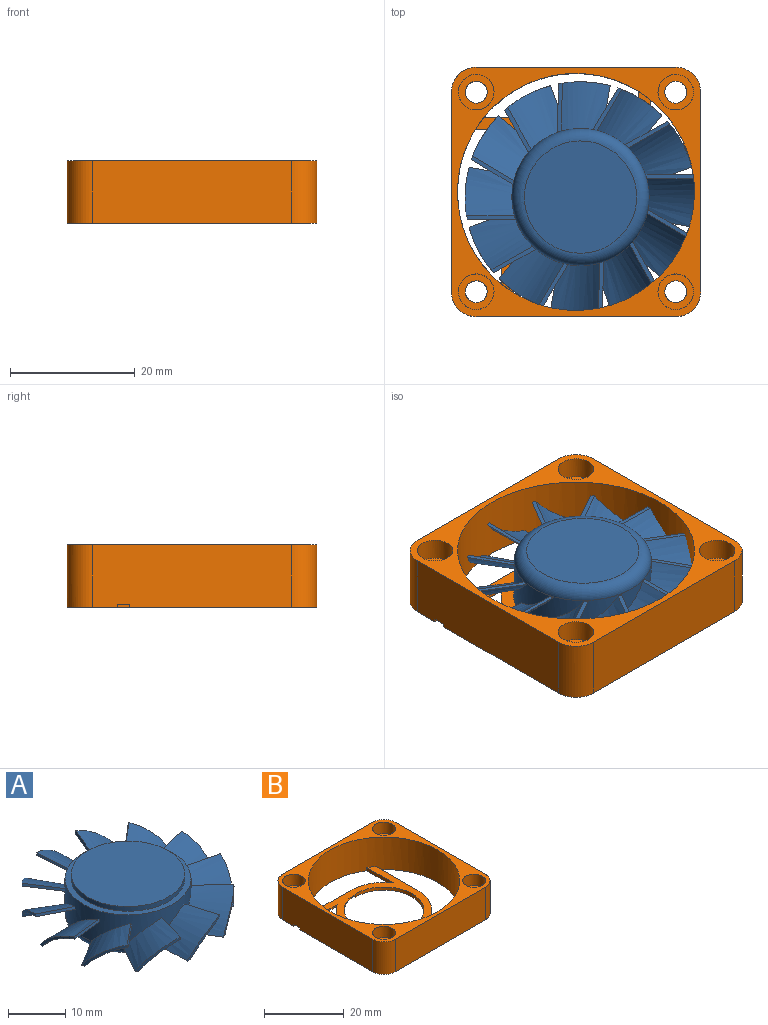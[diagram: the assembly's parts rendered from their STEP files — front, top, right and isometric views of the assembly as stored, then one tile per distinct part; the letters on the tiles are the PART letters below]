
ASSEMBLY  parts=2 mates=1
PART A: 78 faces, bbox 47x47x10.7 mm
  f0: plane 19.83x19.83mm, normal (0,0,1), area 307.3mm2, adj f1
  f1: cylinder r=9.9mm len=19.8mm, axis (0,0,-1), area 62.2mm2, adj f0,f3
  f2: plane 18x18mm, normal (0,0,-1), area 253.9mm2, adj f45
  f3: plane 22.09x22.09mm, normal (0,0,1), area 71mm2, adj f1,f75
  f4: plane 8.6x1.46mm, normal (0,0,-1), area 4.9mm2, adj f15,f46,f47,f48,f75
  f5: plane 7.91x4.96mm, normal (0,0,-1), area 4.9mm2, adj f16,f17,f50,f51,f75
  f6: plane 8.6x1.46mm, normal (0,0,-1), area 4.9mm2, adj f18,f19,f20,f53,f75
  f7: plane 7.54x5.29mm, normal (0,0,-1), area 4.9mm2, adj f21,f22,f23,f55,f75
  f8: plane 7.91x4.96mm, normal (0,0,-1), area 4.9mm2, adj f24,f25,f26,f57,f75
  f9: plane 8.61x1.46mm, normal (0,0,-1), area 4.9mm2, adj f27,f28,f29,f59,f75
  f10: plane 7.54x5.29mm, normal (0,0,-1), area 4.9mm2, adj f30,f31,f61,f62,f75
  f11: plane 7.91x4.96mm, normal (0,0,-1), area 4.9mm2, adj f32,f33,f64,f65,f75
  f12: plane 8.6x1.46mm, normal (0,0,-1), area 4.9mm2, adj f34,f35,f36,f67,f75
  f13: plane 7.54x5.29mm, normal (0,0,-1), area 4.9mm2, adj f37,f38,f39,f69,f75
  f14: plane 7.91x4.96mm, normal (0,0,-1), area 4.9mm2, adj f40,f41,f42,f71,f75
  f15: cylinder r=18.5mm len=8.32mm, axis (0,0,-1), area 5mm2, adj f4,f44,f46,f48
  f16: offset ~17.14x13.81mm, area 71.7mm2, adj f5,f17,f51,f52,f75
  f17: cylinder r=18.5mm len=7.34mm, axis (0,0,-1), area 5mm2, adj f5,f16,f50,f52
  f18: offset ~14.46x10.29mm, area 71.7mm2, adj f6,f19,f53,f54,f75
  f19: cylinder r=18.5mm len=8.32mm, axis (0,0,-1), area 5mm2, adj f6,f18,f20,f54
  f20: offset ~12.66x9.93mm, area 66.2mm2, adj f6,f19,f54,f75
  f21: offset ~16.23x15.39mm, area 71.7mm2, adj f7,f22,f55,f56,f75
  f22: cylinder r=18.5mm len=7.06mm, axis (0,0,-1), area 5mm2, adj f7,f21,f23,f56
  f23: offset ~14.68x14.27mm, area 66.2mm2, adj f7,f22,f56,f75
  f24: offset ~17.14x13.81mm, area 71.7mm2, adj f8,f25,f57,f58,f75
  f25: cylinder r=18.5mm len=7.34mm, axis (0,0,-1), area 5mm2, adj f8,f24,f26,f58
  f26: offset ~15.47x12.9mm, area 66.2mm2, adj f8,f25,f58,f75
  f27: offset ~14.46x10.29mm, area 71.7mm2, adj f9,f28,f59,f60,f75
  f28: cylinder r=18.5mm len=8.32mm, axis (0,0,-1), area 5mm2, adj f9,f27,f29,f60
  f29: offset ~12.66x9.93mm, area 66.2mm2, adj f9,f28,f60,f75
  f30: offset ~16.23x15.39mm, area 71.7mm2, adj f10,f31,f62,f63,f75
  f31: cylinder r=18.5mm len=7.06mm, axis (0,0,-1), area 5mm2, adj f10,f30,f61,f63
  f32: offset ~17.14x13.81mm, area 71.7mm2, adj f11,f33,f65,f66,f75
  f33: cylinder r=18.5mm len=7.34mm, axis (0,0,-1), area 5mm2, adj f11,f32,f64,f66
  f34: offset ~14.46x10.29mm, area 71.7mm2, adj f12,f35,f67,f68,f75
  f35: cylinder r=18.5mm len=8.32mm, axis (0,0,-1), area 5mm2, adj f12,f34,f36,f68
  f36: offset ~12.66x9.93mm, area 66.2mm2, adj f12,f35,f68,f75
  f37: offset ~16.23x15.39mm, area 71.7mm2, adj f13,f38,f69,f70,f75
  f38: cylinder r=18.5mm len=7.06mm, axis (0,0,-1), area 5mm2, adj f13,f37,f39,f70
  f39: offset ~14.68x14.27mm, area 66.2mm2, adj f13,f38,f70,f75
  f40: offset ~17.14x13.81mm, area 71.7mm2, adj f14,f41,f71,f72,f75
  f41: cylinder r=18.5mm len=7.34mm, axis (0,0,-1), area 5mm2, adj f14,f40,f42,f72
  f42: offset ~15.47x12.9mm, area 66.2mm2, adj f14,f41,f72,f75
  f43: plane 7.54x5.29mm, normal (0,0,-1), area 4.9mm2, adj f49,f73,f74,f75,f77
  f44: bspline ~9.04x1.73mm, area 3.8mm2, adj f15,f46,f48,f75
  f45: torus R=9mm, axis (0,0,-1), area 202.6mm2, adj f2,f75
  f46: offset ~12.66x9.93mm, area 64.2mm2, adj f4,f15,f44,f75
  f47: cylinder r=16.24mm len=0.14mm, axis (0.98,0.05,-0.17), area 0mm2, adj f4,f48,f75
  f48: offset ~14.46x10.29mm, area 71.3mm2, adj f4,f15,f44,f47,f75
  f49: cylinder r=16.24mm len=0.13mm, axis (0.82,0.54,-0.17), area 0mm2, adj f43,f73,f75
  f50: offset ~15.47x12.9mm, area 66.2mm2, adj f5,f17,f52,f75
  f51: cylinder r=16.24mm len=0.13mm, axis (0.44,0.88,-0.17), area 0mm2, adj f5,f16,f75
  f52: bspline ~8.7x3.26mm, area 3.8mm2, adj f16,f17,f50,f75
  f53: cylinder r=16.24mm len=0.14mm, axis (-0.05,0.98,-0.17), area 0mm2, adj f6,f18,f75
  f54: bspline ~9.04x1.73mm, area 3.8mm2, adj f18,f19,f20,f75
  f55: cylinder r=16.24mm len=0.13mm, axis (-0.54,0.82,-0.17), area 0mm2, adj f7,f21,f75
  f56: bspline ~7.09x6.02mm, area 3.8mm2, adj f21,f22,f23,f75
  f57: cylinder r=16.25mm len=0.13mm, axis (-0.88,0.44,-0.17), area 0mm2, adj f8,f24
  f58: bspline ~8.7x3.26mm, area 3.8mm2, adj f24,f25,f26,f75
  f59: cylinder r=16.25mm len=0.14mm, axis (-0.98,-0.05,-0.17), area 0mm2, adj f9,f27
  f60: bspline ~9.04x1.73mm, area 3.8mm2, adj f27,f28,f29,f75
  f61: offset ~14.68x14.27mm, area 66.2mm2, adj f10,f31,f63,f75
  f62: cylinder r=16.24mm len=0.13mm, axis (-0.82,-0.54,-0.17), area 0mm2, adj f10,f30,f75
  f63: bspline ~7.09x6.02mm, area 3.8mm2, adj f30,f31,f61,f75
  f64: offset ~15.47x12.9mm, area 66.2mm2, adj f11,f33,f66,f75
  f65: cylinder r=16.24mm len=0.13mm, axis (-0.44,-0.88,-0.17), area 0mm2, adj f11,f32,f75
  f66: bspline ~8.7x3.26mm, area 3.8mm2, adj f32,f33,f64,f75
  f67: cylinder r=16.24mm len=0.14mm, axis (0.05,-0.98,-0.17), area 0mm2, adj f12,f34,f75
  f68: bspline ~9.04x1.73mm, area 3.8mm2, adj f34,f35,f36,f75
  f69: cylinder r=16.24mm len=0.13mm, axis (0.54,-0.82,-0.17), area 0mm2, adj f13,f37,f75
  f70: bspline ~7.09x6.02mm, area 3.8mm2, adj f37,f38,f39,f75
  f71: cylinder r=16.25mm len=0.13mm, axis (0.88,-0.44,-0.17), area 0mm2, adj f14,f40
  f72: bspline ~8.7x3.26mm, area 3.8mm2, adj f40,f41,f42,f75
  f73: offset ~16.23x15.39mm, area 71.7mm2, adj f43,f49,f74,f75,f76
  f74: cylinder r=18.5mm len=7.06mm, axis (0,0,-1), area 5mm2, adj f43,f73,f76,f77
  f75: cylinder r=11mm len=22mm, axis (0,0,-1), area 195.2mm2, adj f3,f4,f5,f6,f7,f8,f9,f10
  f76: bspline ~7.09x6.02mm, area 3.8mm2, adj f73,f74,f75,f77
  f77: offset ~11.35x10.77mm, area 66.2mm2, adj f43,f74,f75,f76
PART B: 42 faces, bbox 40.8x40.8x10.8 mm
  f0: plane 6.46x6.46mm, normal (0,0,1), area 16mm2, adj f7,f8
  f1: plane 6.46x6.46mm, normal (0,0,1), area 16mm2, adj f6,f9
  f2: plane 6.46x6.46mm, normal (0,0,1), area 16mm2, adj f5,f10
  f3: plane 6.46x6.46mm, normal (0,0,1), area 16mm2, adj f4,f11
  f4: cylinder r=2.85mm len=5.7mm, axis (0,0,-1), area 62.7mm2, adj f3,f37
  f5: cylinder r=2.85mm len=5.7mm, axis (0,0,-1), area 62.7mm2, adj f2,f37
  f6: cylinder r=2.85mm len=5.7mm, axis (0,0,-1), area 62.7mm2, adj f1,f37
  f7: cylinder r=2.85mm len=5.7mm, axis (0,0,-1), area 62.7mm2, adj f0,f37
  f8: cylinder r=1.75mm len=6.5mm, axis (0,0,-1), area 71.5mm2, adj f0,f39
  f9: cylinder r=1.75mm len=6.5mm, axis (0,0,-1), area 71.5mm2, adj f1,f39
  f10: cylinder r=1.75mm len=6.5mm, axis (0,0,-1), area 71.5mm2, adj f2,f39
  f11: cylinder r=1.75mm len=6.5mm, axis (0,0,-1), area 71.5mm2, adj f3,f39
  f12: cylinder r=4mm len=10mm, axis (0,0,-1), area 62.8mm2, adj f22,f23,f37,f39
  f13: cylinder r=4mm len=10mm, axis (0,0,-1), area 62.8mm2, adj f23,f24,f37,f39
  f14: cylinder r=12mm len=10mm, axis (0,0,-1), area 11.8mm2, adj f18,f20,f25,f26,f39
  f15: cylinder r=10mm len=20mm, axis (0,0,1), area 59.2mm2, adj f18,f26,f27,f34,f39
  f16: cylinder r=12mm len=10mm, axis (0,0,-1), area 11.8mm2, adj f18,f21,f27,f28,f39
  f17: cylinder r=12mm len=10mm, axis (0,0,-1), area 11.8mm2, adj f18,f29,f30,f39
  f18: plane 32.4x32.4mm, normal (0,0,1), area 224.9mm2, adj f14,f15,f16,f17,f19,f20,f21,f25
  f19: cylinder r=12mm len=10mm, axis (0,0,-1), area 11.8mm2, adj f18,f31,f32,f39
  f20: plane 9.52x0.5mm, normal (0,-1,0), area 4.8mm2, adj f14,f18,f33,f34
  f21: plane 14.73x0.5mm, normal (0,1,0), area 7.4mm2, adj f16,f18,f33,f34
  f22: plane 32x10mm, normal (0,1,0), area 320mm2, adj f12,f37,f38,f39
  f23: plane 32x10mm, normal (1,0,0), area 320mm2, adj f12,f13,f37,f39
  f24: plane 32x10mm, normal (0,-1,0), area 320mm2, adj f13,f36,f37,f39
  f25: plane 14.73x1mm, normal (-1,0,0), area 14.7mm2, adj f14,f18,f33,f39
  f26: plane 2.52x0.5mm, normal (1,0,0), area 1.3mm2, adj f14,f15,f34,f39
  f27: plane 2x0.5mm, normal (-1,0,0), area 1mm2, adj f15,f16,f34,f39
  f28: plane 9.52x1mm, normal (-1,0,0), area 9.5mm2, adj f16,f18,f33,f39
  f29: plane 14.73x1mm, normal (1,0,0), area 14.7mm2, adj f17,f18,f33,f39
  f30: plane 9.52x1mm, normal (0,1,0), area 9.5mm2, adj f17,f18,f33,f39
  f31: plane 9.52x1mm, normal (1,0,0), area 9.5mm2, adj f18,f19,f33,f39
  f32: plane 14.73x1mm, normal (0,-1,0), area 14.7mm2, adj f18,f19,f33,f39
  f33: cylinder r=19mm len=38mm, axis (0,0,1), area 1184mm2, adj f18,f20,f21,f25,f28,f29,f30,f31
  f34: plane 20.07x4.59mm, normal (0,0,-1), area 45.2mm2, adj f15,f20,f21,f26,f27,f35,f40,f41
  f35: plane 3.84x0.5mm, normal (0,1,0), area 1.9mm2, adj f33,f34,f39,f41
  f36: cylinder r=4mm len=10mm, axis (0,0,-1), area 62.8mm2, adj f24,f37,f39,f41
  f37: plane 40.12x40.12mm, normal (0,0,1), area 350.4mm2, adj f4,f5,f6,f7,f12,f13,f22,f23
  f38: cylinder r=4mm len=10mm, axis (0,0,-1), area 62.8mm2, adj f22,f37,f39,f41
  f39: plane 40.02x40.02mm, normal (0,0,-1), area 752.4mm2, adj f8,f9,f10,f11,f12,f13,f14,f15
  f40: plane 5.27x0.5mm, normal (0,-1,0), area 2.6mm2, adj f33,f34,f39,f41
  f41: plane 32x10mm, normal (-1,0,0), area 319mm2, adj f34,f35,f36,f37,f38,f39,f40
PLACE A rot(axis=(0.71,-0.71,0),180deg) t=(24.22,26,18.88)mm
PLACE B t=(43.51,6.82,8.88)mm
MATE revolute B.f39 <-> A.f38  axis (0,0,-1) through (24.22,26,8.88)mm
